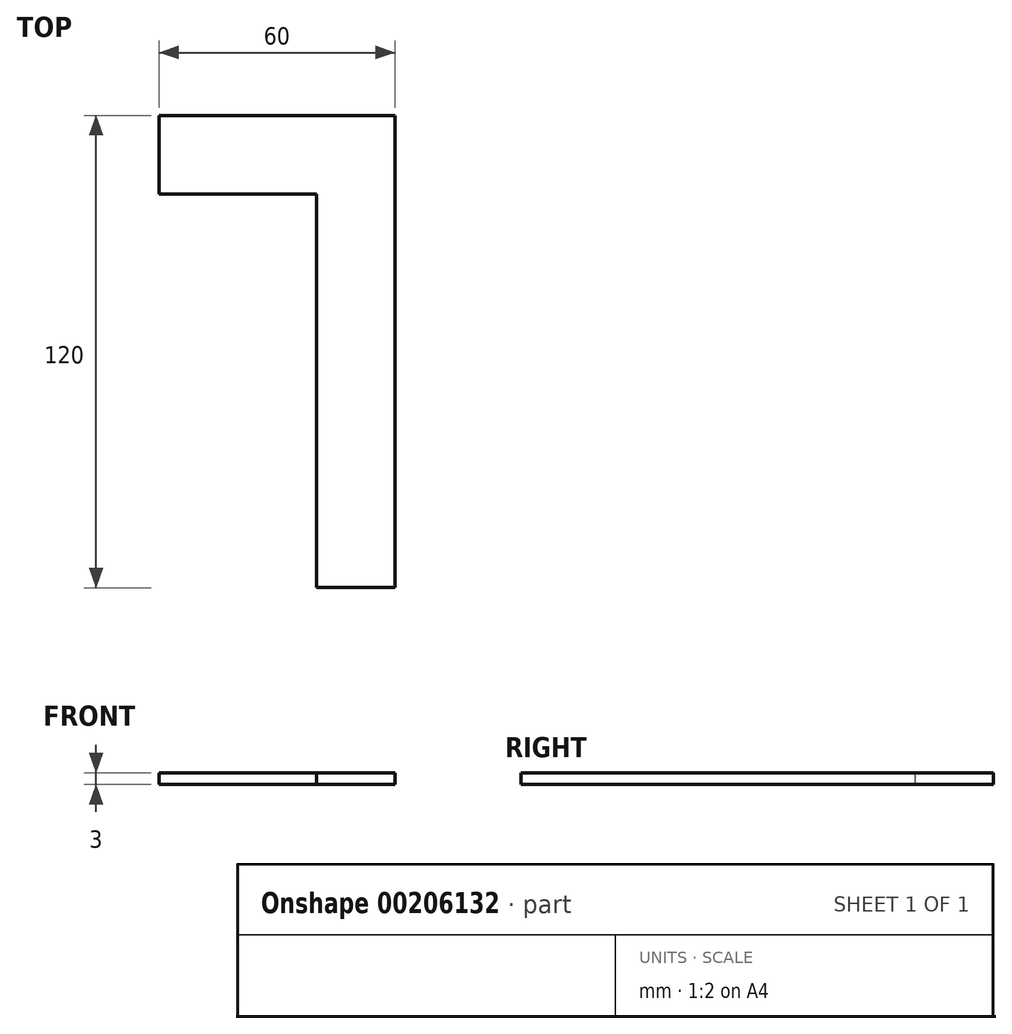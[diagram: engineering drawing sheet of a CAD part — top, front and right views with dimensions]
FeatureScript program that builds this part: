
annotation { "Feature Type Name" : "Feature", "Feature Type Description" : "" }
export const myFeature = defineFeature(function(context is Context, id is Id, definition is map)
    precondition{}
    {
        {
            var Q0;
            Q0=qCreatedBy(makeId("Top.planeOp"),FACE);
            var sketch = newSketch(context, id + "F0", { "sketchPlane" : qUnion([Q0])});
            skLineSegment(sketch, "E0.bottom", {"start": v(-40, 41.63) * mm, "end": v(20, 41.63) * mm});
            skLineSegment(sketch, "E0.top", {"start": v(-40, 21.63) * mm, "end": v(20, 21.63) * mm});
            skLineSegment(sketch, "E0.left", {"start": v(-40, 41.63) * mm, "end": v(-40, 21.63) * mm});
            skLineSegment(sketch, "E0.right", {"start": v(20, 41.63) * mm, "end": v(20, 21.63) * mm});
            skLineSegment(sketch, "E1.bottom", {"start": v(20, 21.63) * mm, "end": v(0, 21.63) * mm});
            skLineSegment(sketch, "E1.top", {"start": v(20, -78.37) * mm, "end": v(0, -78.37) * mm});
            skLineSegment(sketch, "E1.left", {"start": v(20, 21.63) * mm, "end": v(20, -78.37) * mm});
            skLineSegment(sketch, "E1.right", {"start": v(0, 21.63) * mm, "end": v(0, -78.37) * mm});
            skSolve(sketch);
        }
        {
            var Q0;
            Q0 = qSketchRegion(id + "F0", true);
            extrude(context, id + "F1", {"entities" : qUnion([Q0]), "depth" : 3 * mm});
        }
    });
